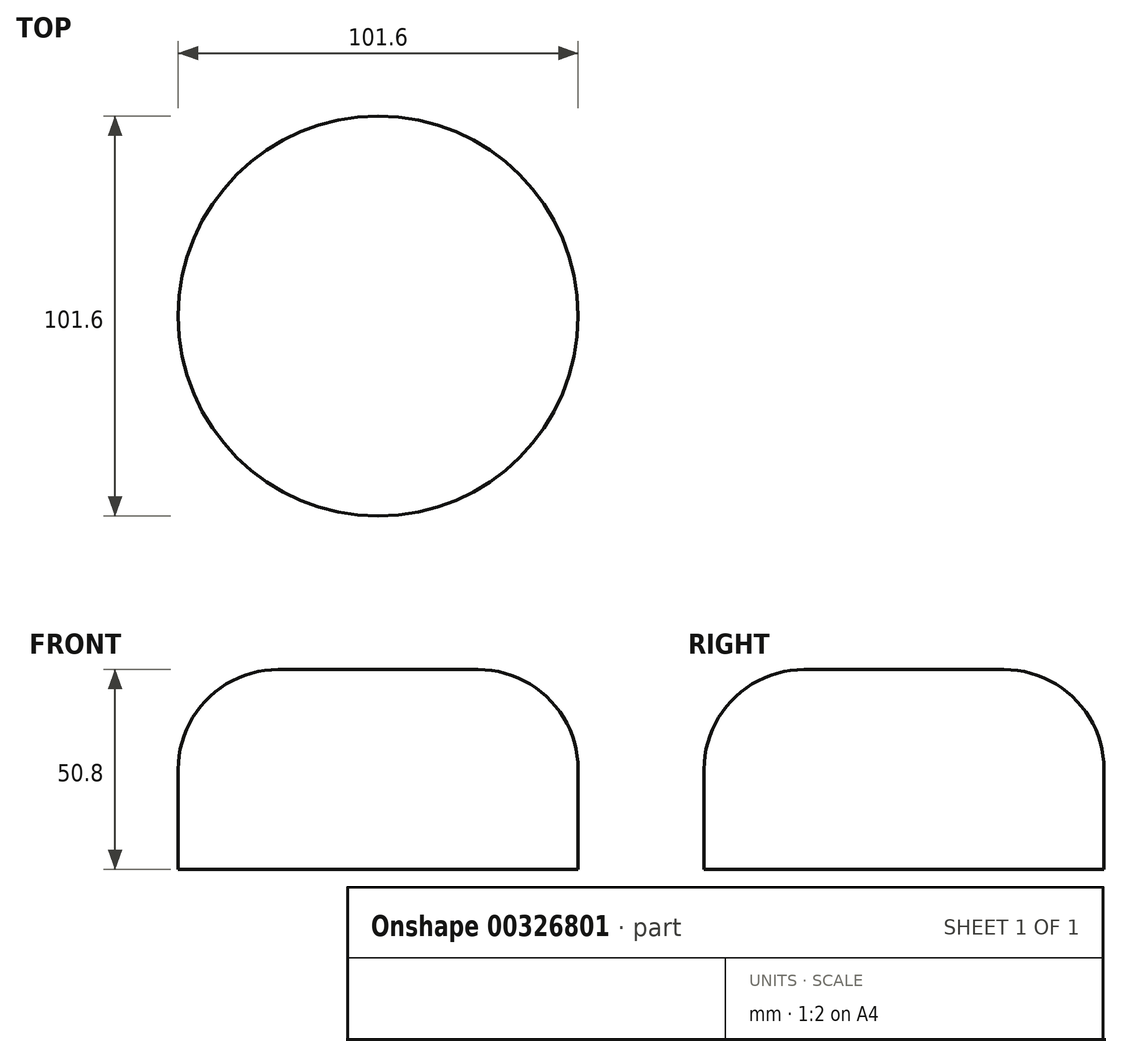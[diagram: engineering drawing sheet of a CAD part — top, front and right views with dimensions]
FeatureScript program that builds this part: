
annotation { "Feature Type Name" : "Feature", "Feature Type Description" : "" }
export const myFeature = defineFeature(function(context is Context, id is Id, definition is map)
    precondition{}
    {
        {
            var Q0;
            Q0=qCreatedBy(makeId("Front.planeOp"),FACE);
            var sketch = newSketch(context, id + "F0", { "sketchPlane" : qUnion([Q0])});
            skLineSegment(sketch, "E0.bottom", {"start": v(-20.66, -35.84) * mm, "end": v(30.14, -35.84) * mm});
            skLineSegment(sketch, "E0.top", {"start": v(-20.66, 14.96) * mm, "end": v(4.74, 14.96) * mm});
            skLineSegment(sketch, "E0.left", {"start": v(-20.66, -35.84) * mm, "end": v(-20.66, 14.96) * mm});
            skLineSegment(sketch, "E0.right", {"start": v(30.14, -35.84) * mm, "end": v(30.14, -10.44) * mm});
            skPoint(sketch, "E1.visualSharp", {"position": v(30.14, 14.96) * mm});
            skArc(sketch, "E1.filletArc", {"start": v(30.14, -10.44) * mm, "mid": v(22.7, 7.52) * mm, "end": v(4.74, 14.96) * mm});
            skLineSegment(sketch, "E2", {"start": v(30.14, -10.44) * mm, "end": v(30.14, -10.44) * mm});
            skSolve(sketch);
        }
        {
            var Q0;
            Q0=makeQuery(id+"F0.imprint","IMPRINT",FACE,{"disambiguationData":[TD([[makeQuery(id+"F0.imprint","IMPRINT",EDGE,{"derivedFrom":sQuery(id+"F0.wireOp",EDGE,"E0.bottom")}),1.0]])]});
            var Q1;
            Q1=sQuery(id+"F0.wireOp",EDGE,"E0.left");
            revolve(context, id + "F1", {"entities" : qUnion([Q0]), "axis" : qUnion([Q1]), "revolveType" : RevolveType.ONE_DIRECTION, "angle" : 360 * degree});
        }
    });
